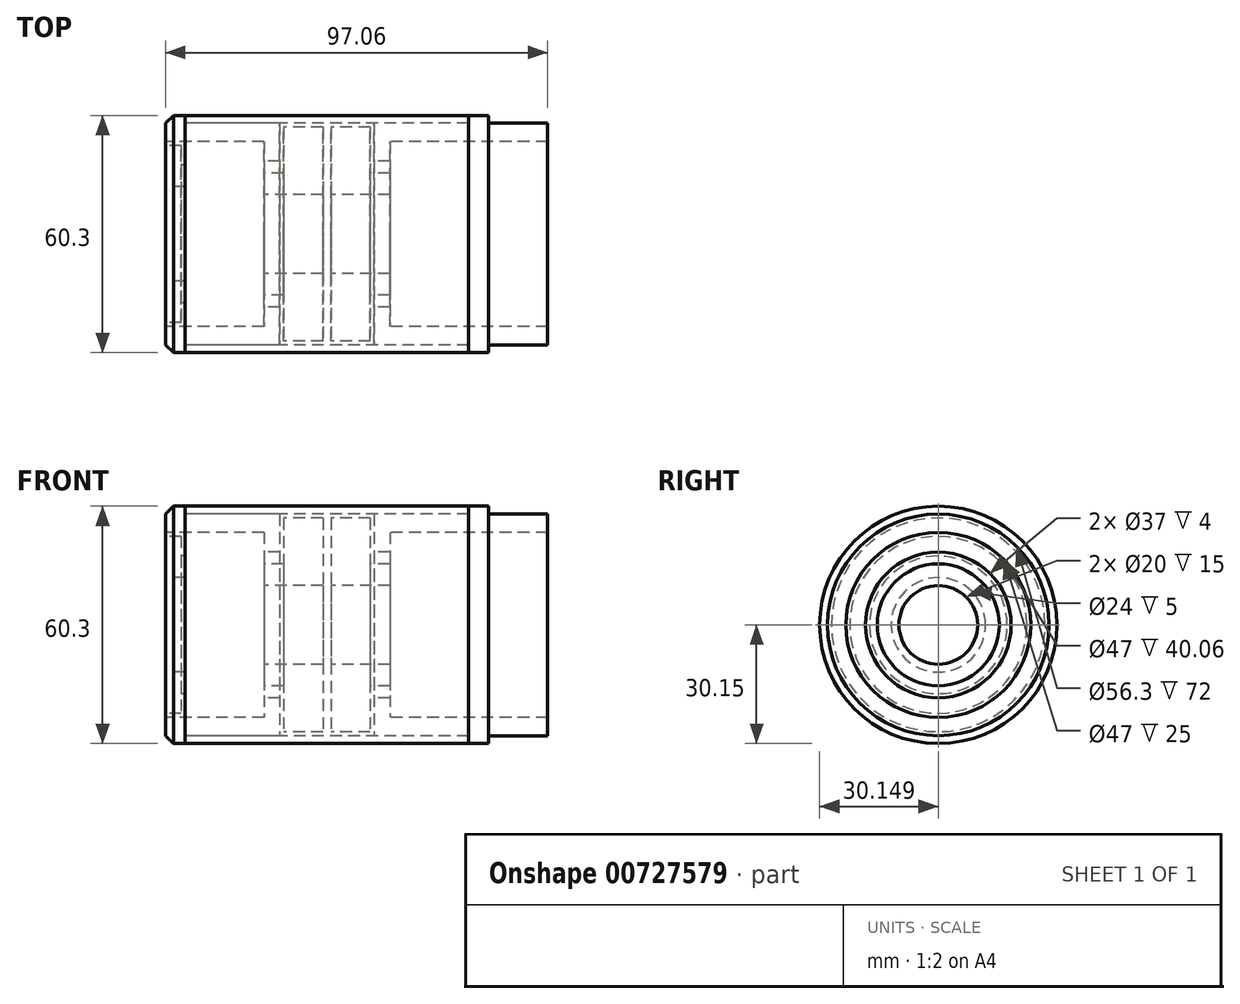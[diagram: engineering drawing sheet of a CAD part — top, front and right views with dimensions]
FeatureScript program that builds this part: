
annotation { "Feature Type Name" : "Feature", "Feature Type Description" : "" }
export const myFeature = defineFeature(function(context is Context, id is Id, definition is map)
    precondition{}
    {
        {
            var Q0;
            Q0=qCreatedBy(makeId("Top.planeOp"),FACE);
            var sketch = newSketch(context, id + "F0", { "sketchPlane" : qUnion([Q0])});
            skLineSegment(sketch, "E0", {"start": v(26.1, 58.09) * mm, "end": v(53.75, 58.09) * mm, "construction": true});
            skLineSegment(sketch, "E1", {"start": v(53.75, 88.24) * mm, "end": v(53.75, 81.59) * mm});
            skLineSegment(sketch, "E2", {"start": v(53.75, 81.59) * mm, "end": v(78.75, 81.59) * mm});
            skLineSegment(sketch, "E3", {"start": v(78.75, 81.59) * mm, "end": v(78.75, 76.59) * mm});
            skLineSegment(sketch, "E4", {"start": v(78.75, 76.59) * mm, "end": v(82.75, 76.59) * mm});
            skLineSegment(sketch, "E5", {"start": v(82.75, 76.59) * mm, "end": v(82.75, 86.24) * mm});
            skLineSegment(sketch, "E6", {"start": v(82.75, 86.24) * mm, "end": v(58.75, 86.24) * mm});
            skLineSegment(sketch, "E7", {"start": v(58.75, 86.24) * mm, "end": v(58.75, 88.24) * mm});
            skLineSegment(sketch, "E8", {"start": v(58.75, 88.24) * mm, "end": v(53.75, 88.24) * mm});
            skLineSegment(sketch, "E9", {"start": v(78.75, 58.09) * mm, "end": v(78.75, 73.59) * mm});
            skLineSegment(sketch, "E10", {"start": v(78.75, 73.59) * mm, "end": v(83.75, 73.59) * mm});
            skLineSegment(sketch, "E11", {"start": v(83.75, 73.59) * mm, "end": v(83.75, 85.24) * mm});
            skLineSegment(sketch, "E12", {"start": v(83.75, 85.24) * mm, "end": v(93.75, 85.24) * mm});
            skLineSegment(sketch, "E13", {"start": v(93.75, 85.24) * mm, "end": v(93.75, 58.09) * mm});
            skLineSegment(sketch, "E14", {"start": v(93.75, 58.09) * mm, "end": v(78.75, 58.09) * mm});
            skLineSegment(sketch, "E15", {"start": v(94.75, 92.46) * mm, "end": v(94.75, 46.04) * mm, "construction": true});
            skLineSegment(sketch, "E16.MirrorCS", {"start": v(110.75, 73.59) * mm, "end": v(105.75, 73.59) * mm});
            skLineSegment(sketch, "E17.MirrorCS", {"start": v(95.75, 58.09) * mm, "end": v(110.75, 58.09) * mm});
            skLineSegment(sketch, "E18.MirrorCS", {"start": v(110.75, 58.09) * mm, "end": v(110.75, 73.59) * mm});
            skLineSegment(sketch, "E19.MirrorCS", {"start": v(95.75, 85.24) * mm, "end": v(95.75, 58.09) * mm});
            skLineSegment(sketch, "E20.MirrorCS", {"start": v(105.75, 85.24) * mm, "end": v(95.75, 85.24) * mm});
            skLineSegment(sketch, "E21.MirrorCS", {"start": v(105.75, 73.59) * mm, "end": v(105.75, 85.24) * mm});
            skLineSegment(sketch, "E22.MirrorCS", {"start": v(106.75, 76.59) * mm, "end": v(106.75, 86.24) * mm});
            skLineSegment(sketch, "E23.MirrorCS", {"start": v(110.75, 76.59) * mm, "end": v(106.75, 76.59) * mm});
            skLineSegment(sketch, "E24.MirrorCS", {"start": v(110.75, 81.59) * mm, "end": v(110.75, 76.59) * mm});
            skLineSegment(sketch, "E25.MirrorCS", {"start": v(130.75, 88.24) * mm, "end": v(135.75, 88.24) * mm});
            skLineSegment(sketch, "E26.MirrorCS", {"start": v(130.75, 86.24) * mm, "end": v(130.75, 88.24) * mm});
            skLineSegment(sketch, "E27.MirrorCS", {"start": v(106.75, 86.24) * mm, "end": v(130.75, 86.24) * mm});
            skLineSegment(sketch, "E28.MirrorCS", {"start": v(135.75, 81.59) * mm, "end": v(110.75, 81.59) * mm});
            skLineSegment(sketch, "E29", {"start": v(135.75, 88.24) * mm, "end": v(135.75, 86.24) * mm});
            skLineSegment(sketch, "E30", {"start": v(53.75, 70.09) * mm, "end": v(53.75, 80.59) * mm});
            skLineSegment(sketch, "E31", {"start": v(53.75, 80.59) * mm, "end": v(57.75, 80.59) * mm});
            skLineSegment(sketch, "E32", {"start": v(58.75, 76.34) * mm, "end": v(58.75, 76.34) * mm});
            skLineSegment(sketch, "E33", {"start": v(58.75, 75.58) * mm, "end": v(58.75, 70.09) * mm});
            skLineSegment(sketch, "E34", {"start": v(135.75, 86.24) * mm, "end": v(150.8, 86.24) * mm});
            skLineSegment(sketch, "E35", {"start": v(150.8, 86.24) * mm, "end": v(150.8, 81.59) * mm});
            skLineSegment(sketch, "E36", {"start": v(150.8, 81.59) * mm, "end": v(135.75, 81.59) * mm});
            skLineSegment(sketch, "E37.bottom", {"start": v(58.75, 88.24) * mm, "end": v(130.75, 88.24) * mm});
            skLineSegment(sketch, "E37.top", {"start": v(58.75, 86.24) * mm, "end": v(130.75, 86.24) * mm});
            skLineSegment(sketch, "E37.left", {"start": v(58.75, 88.24) * mm, "end": v(58.75, 86.24) * mm});
            skLineSegment(sketch, "E37.right", {"start": v(130.75, 88.24) * mm, "end": v(130.75, 86.24) * mm});
            skLineSegment(sketch, "E38", {"start": v(57.75, 80.59) * mm, "end": v(57.75, 75.58) * mm});
            skLineSegment(sketch, "E39", {"start": v(57.75, 75.58) * mm, "end": v(58.75, 75.58) * mm});
            skLineSegment(sketch, "E40.trimOffspring", {"start": v(58.75, 58.09) * mm, "end": v(123.59, 58.09) * mm, "construction": true});
            skLineSegment(sketch, "E41", {"start": v(58.75, 70.09) * mm, "end": v(53.75, 70.09) * mm});
            skLineSegment(sketch, "E42", {"start": v(117.78, 68.09) * mm, "end": v(66.44, 68.09) * mm});
            skSolve(sketch);
        }
        {
            var Q0;
            Q0=makeQuery(id+"F0.imprint","IMPRINT",FACE,{"disambiguationData":[TD([[makeQuery(id+"F0.imprint","IMPRINT",EDGE,{"derivedFrom":sQuery(id+"F0.wireOp",EDGE,"E16.MirrorCS")}),1.0]])]});
            var Q1;
            Q1=makeQuery(id+"F0.imprint","IMPRINT",FACE,{"disambiguationData":[TD([[makeQuery(id+"F0.imprint","IMPRINT",EDGE,{"derivedFrom":sQuery(id+"F0.wireOp",EDGE,"E22.MirrorCS")}),-1.0]])]});
            var Q2;
            Q2=makeQuery(id+"F0.imprint","IMPRINT",FACE,{"disambiguationData":[TD([[makeQuery(id+"F0.imprint","IMPRINT",EDGE,{"derivedFrom":sQuery(id+"F0.wireOp",EDGE,"E1")}),1.0]])]});
            var Q3;
            {var subQ1=sQuery(id+"F0.wireOp",EDGE,"E10");Q3=makeQuery(id+"F0.imprint","IMPRINT",FACE,{"disambiguationData":[TD([[makeQuery(id+"F0.imprint","IMPRINT",EDGE,{"derivedFrom":subQ1}),-1.0]])]});}
            var Q4;
            Q4=sQuery(id+"F0.wireOp",EDGE,"E0");
            revolve(context, id + "F1", {"surfaceOperationType" : NewSurfaceOperationType.NEW, "entities" : qUnion([Q0, Q1, Q2, Q3]), "axis" : qUnion([Q4]), "revolveType" : RevolveType.FULL});
        }
        {
            var Q0;
            Q0=makeQuery(id+"F0.imprint","IMPRINT",FACE,{"disambiguationData":[TD([[makeQuery(id+"F0.imprint","IMPRINT",EDGE,{"derivedFrom":sQuery(id+"F0.wireOp",EDGE,"E37.bottom")}),-1.0]])]});
            var Q1;
            Q1=sQuery(id+"F0.wireOp",EDGE,"E0");
            revolve(context, id + "F2", {"surfaceOperationType" : NewSurfaceOperationType.NEW, "entities" : qUnion([Q0]), "axis" : qUnion([Q1]), "revolveType" : RevolveType.FULL});
        }
        {
            var Q0;
            Q0=makeQuery(id+"F1.opRevolve","SWEPT_EDGE",EDGE,{"disambiguationData":[OSD([sQuery(id+"F0.wireOp",EDGE,"E1"),sQuery(id+"F0.wireOp",EDGE,"E8")])]});
            chamfer(context, id + "F3", {"entities" : qUnion([Q0]), "width" : 2 * mm, "tangentPropagation" : true});
        }
        {
            var Q0;
            {var subQ7=sQuery(id+"F0.wireOp",EDGE,"E38");Q0=makeQuery(id+"F0.imprint","IMPRINT",FACE,{"disambiguationData":[TD([[makeQuery(id+"F0.imprint","IMPRINT",EDGE,{"derivedFrom":subQ7}),-1.0]])]});}
            var Q1;
            Q1=sQuery(id+"F0.wireOp",EDGE,"E0");
            revolve(context, id + "F4", {"surfaceOperationType" : NewSurfaceOperationType.NEW, "entities" : qUnion([Q0]), "axis" : qUnion([Q1]), "revolveType" : RevolveType.FULL});
        }
    });
